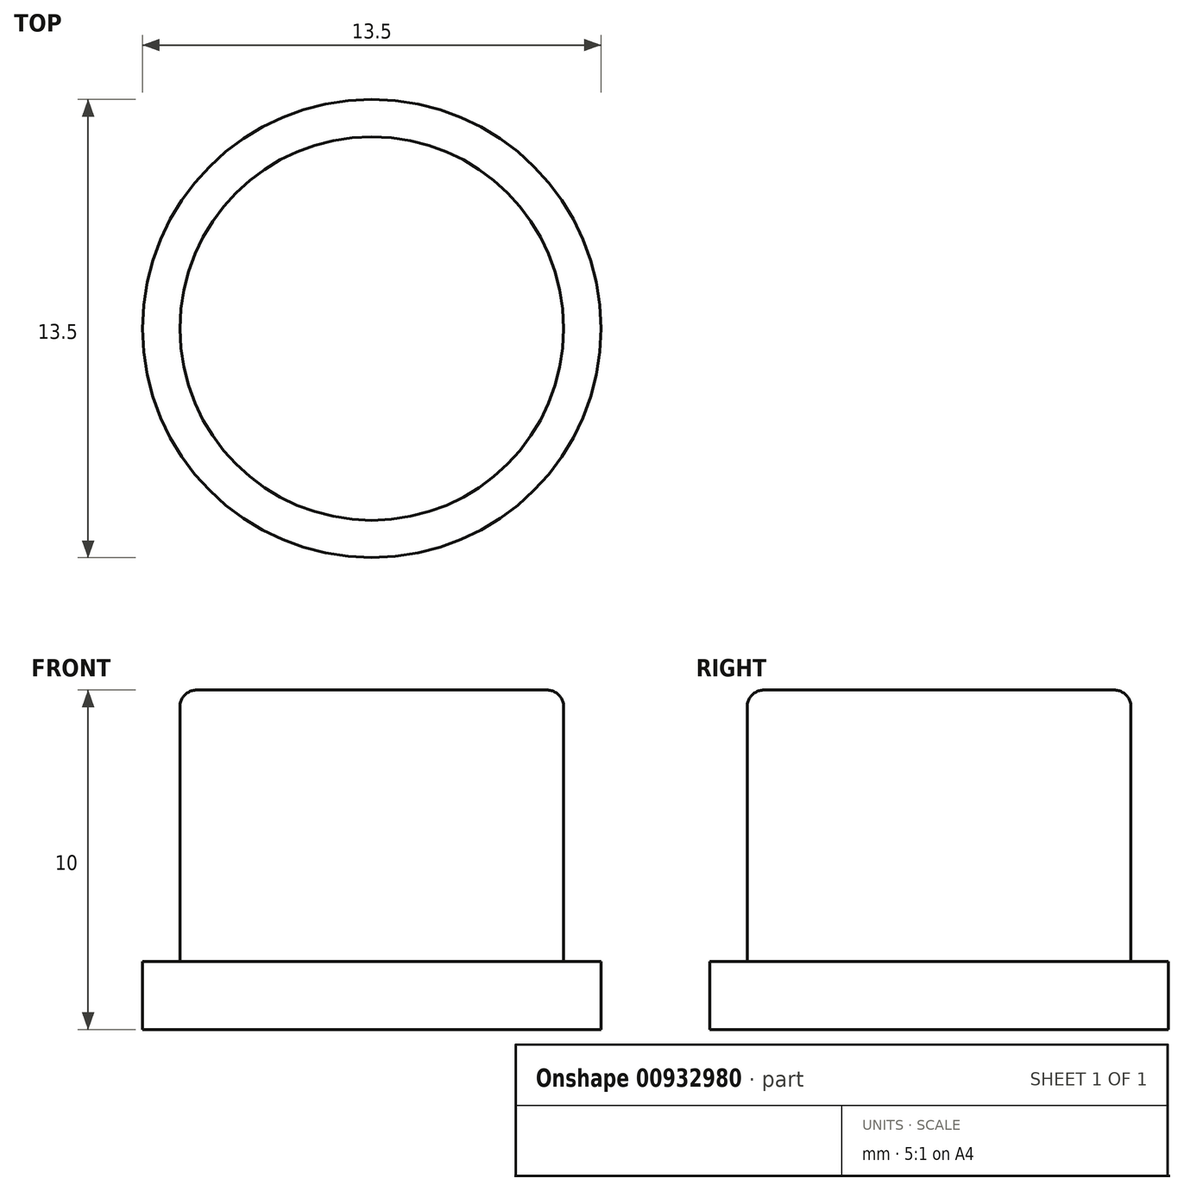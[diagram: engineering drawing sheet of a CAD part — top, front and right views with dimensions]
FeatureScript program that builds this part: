
annotation { "Feature Type Name" : "Feature", "Feature Type Description" : "" }
export const myFeature = defineFeature(function(context is Context, id is Id, definition is map)
    precondition{}
    {
        {
            var Q0;
            Q0=qCreatedBy(makeId("Top.planeOp"),FACE);
            var sketch = newSketch(context, id + "F0", { "sketchPlane" : qUnion([Q0])});
            skCircle(sketch, "E0", {"center": v(0, 0) * mm, "radius": 5.65 * mm});
            skCircle(sketch, "E1", {"center": v(0, 0) * mm, "radius": 6.75 * mm});
            skText(sketch, "E2", { "text": "Down", "fontName": "OpenSans-Bold.ttf"});
            const initialGuessF0  = {"E2": [-0.0048, -0.00122, 1, 0, 0.00239]};
            skSetInitialGuess(sketch, initialGuessF0);
            skSolve(sketch);
        }
        {
            var Q0;
            Q0=makeQuery(id+"F0.imprint","IMPRINT",FACE,{"disambiguationData":[TD([[makeQuery(id+"F0.imprint","IMPRINT",EDGE,{"derivedFrom":sQuery(id+"F0.wireOp",EDGE,"E0")}),1.0]])]});
            var Q1;
            Q1=makeQuery(id+"F0.imprint","IMPRINT",FACE,{"disambiguationData":[TD([[makeQuery(id+"F0.imprint","IMPRINT",EDGE,{"derivedFrom":sQuery(id+"F0.wireOp",EDGE,"ea572825-a978-4dcc-8ec6-78ba32318728.sketch_text.stroke-7")}),1.0]])]});
            var Q2;
            Q2=makeQuery(id+"F0.imprint","IMPRINT",FACE,{"disambiguationData":[TD([[makeQuery(id+"F0.imprint","IMPRINT",EDGE,{"derivedFrom":sQuery(id+"F0.wireOp",EDGE,"ea572825-a978-4dcc-8ec6-78ba32318728.sketch_text.stroke-0")}),-1.0]])]});
            var Q3;
            Q3=makeQuery(id+"F0.imprint","IMPRINT",FACE,{"disambiguationData":[TD([[makeQuery(id+"F0.imprint","IMPRINT",EDGE,{"derivedFrom":sQuery(id+"F0.wireOp",EDGE,"ea572825-a978-4dcc-8ec6-78ba32318728.sketch_text.stroke-12")}),-1.0]])]});
            var Q4;
            Q4=makeQuery(id+"F0.imprint","IMPRINT",FACE,{"disambiguationData":[TD([[makeQuery(id+"F0.imprint","IMPRINT",EDGE,{"derivedFrom":sQuery(id+"F0.wireOp",EDGE,"ea572825-a978-4dcc-8ec6-78ba32318728.sketch_text.stroke-12")}),1.0]])]});
            var Q5;
            Q5=makeQuery(id+"F0.imprint","IMPRINT",FACE,{"disambiguationData":[TD([[makeQuery(id+"F0.imprint","IMPRINT",EDGE,{"derivedFrom":sQuery(id+"F0.wireOp",EDGE,"ea572825-a978-4dcc-8ec6-78ba32318728.sketch_text.stroke-56")}),-1.0]])]});
            var Q6;
            Q6=makeQuery(id+"F0.imprint","IMPRINT",FACE,{"disambiguationData":[TD([[makeQuery(id+"F0.imprint","IMPRINT",EDGE,{"derivedFrom":sQuery(id+"F0.wireOp",EDGE,"ea572825-a978-4dcc-8ec6-78ba32318728.sketch_text.stroke-30")}),-1.0]])]});
            var Q7;
            Q7=makeQuery(id+"F0.imprint","IMPRINT",FACE,{"disambiguationData":[TD([[makeQuery(id+"F0.imprint","IMPRINT",EDGE,{"derivedFrom":sQuery(id+"F0.wireOp",EDGE,"E2.sketch_text.stroke-0")}),-1.0]])]});
            var Q8;
            Q8=makeQuery(id+"F0.imprint","IMPRINT",FACE,{"disambiguationData":[TD([[makeQuery(id+"F0.imprint","IMPRINT",EDGE,{"derivedFrom":sQuery(id+"F0.wireOp",EDGE,"E2.sketch_text.stroke-7")}),1.0]])]});
            var Q9;
            Q9=makeQuery(id+"F0.imprint","IMPRINT",FACE,{"disambiguationData":[TD([[makeQuery(id+"F0.imprint","IMPRINT",EDGE,{"derivedFrom":sQuery(id+"F0.wireOp",EDGE,"E2.sketch_text.stroke-12")}),-1.0]])]});
            var Q10;
            Q10=makeQuery(id+"F0.imprint","IMPRINT",FACE,{"disambiguationData":[TD([[makeQuery(id+"F0.imprint","IMPRINT",EDGE,{"derivedFrom":sQuery(id+"F0.wireOp",EDGE,"E2.sketch_text.stroke-12")}),1.0]])]});
            var Q11;
            Q11=makeQuery(id+"F0.imprint","IMPRINT",FACE,{"disambiguationData":[TD([[makeQuery(id+"F0.imprint","IMPRINT",EDGE,{"derivedFrom":sQuery(id+"F0.wireOp",EDGE,"E2.sketch_text.stroke-30")}),-1.0]])]});
            var Q12;
            Q12=makeQuery(id+"F0.imprint","IMPRINT",FACE,{"disambiguationData":[TD([[makeQuery(id+"F0.imprint","IMPRINT",EDGE,{"derivedFrom":sQuery(id+"F0.wireOp",EDGE,"E2.sketch_text.stroke-56")}),-1.0]])]});
            extrude(context, id + "F1", {"entities" : qUnion([Q0, Q1, Q2, Q3, Q4, Q5, Q6, Q7, Q8, Q9, Q10, Q11, Q12]), "depth" : 10 * mm, "offsetDistance" : 25 * mm});
        }
        {
            var Q0;
            Q0=makeQuery(id+"F0.imprint","IMPRINT",FACE,{"disambiguationData":[TD([[makeQuery(id+"F0.imprint","IMPRINT",EDGE,{"derivedFrom":sQuery(id+"F0.wireOp",EDGE,"E0")}),-1.0]])]});
            extrude(context, id + "F2", {"entities" : qUnion([Q0]), "operationType" : NewBodyOperationType.ADD, "depth" : 2 * mm, "offsetDistance" : 25 * mm});
        }
        {
            var Q0;
            Q0=makeQuery(id+"F1.opExtrude","CAP_EDGE",EDGE,{"disambiguationData":[OSD([sQuery(id+"F0.wireOp",EDGE,"E0")])],"isStart":false});
            fillet(context, id + "F3", {"entities" : qUnion([Q0]), "radius" : .5 * mm, "tangentPropagation" : true, "allowEdgeOverflow" : false});
        }
    });
